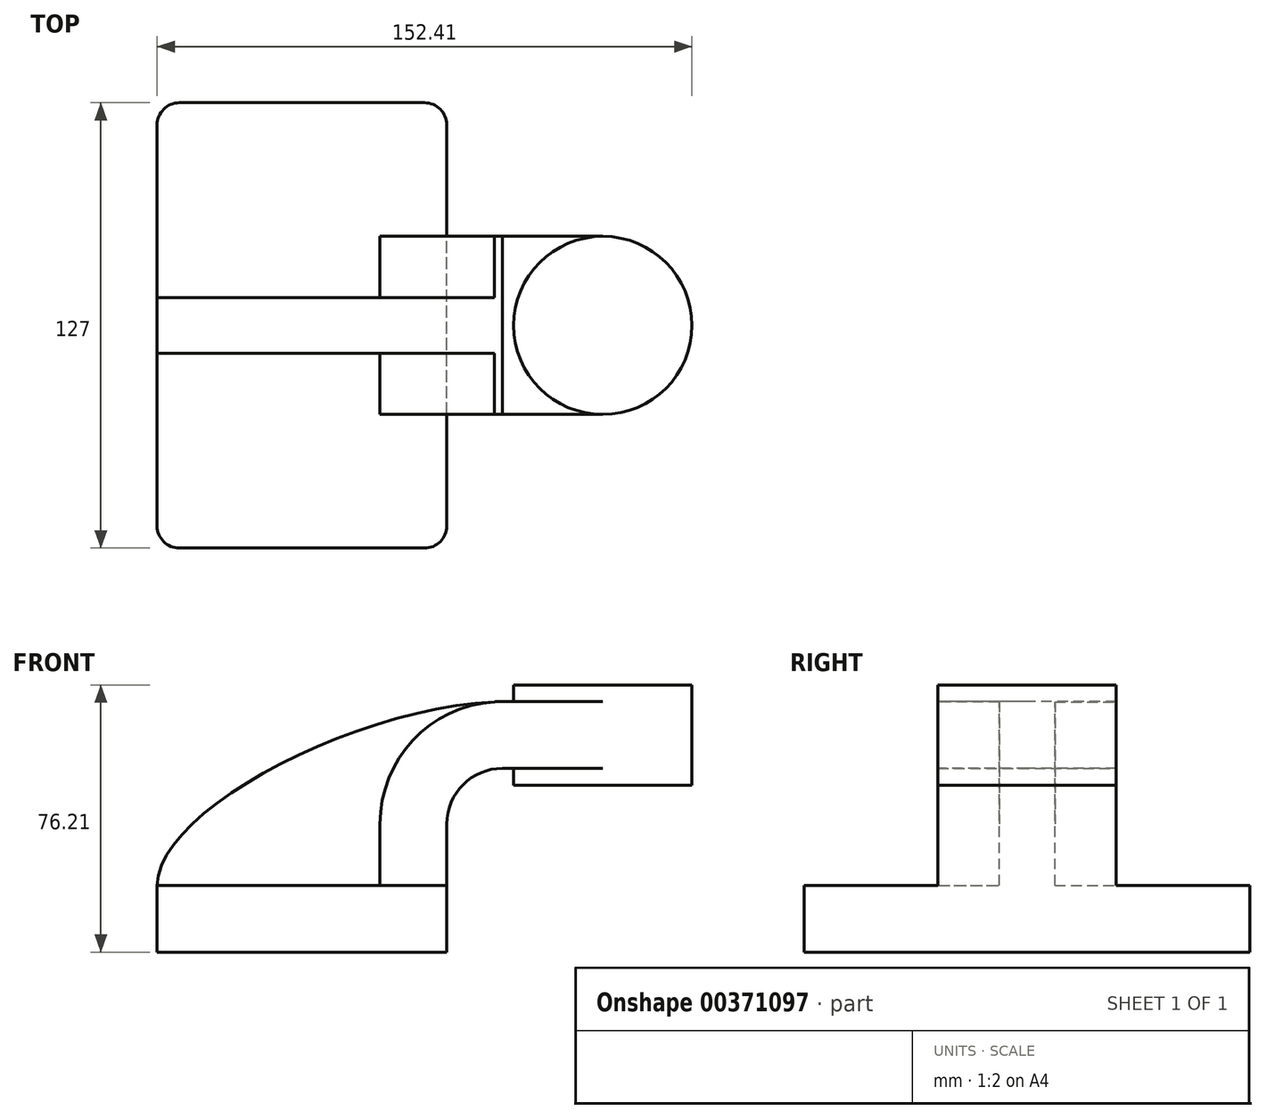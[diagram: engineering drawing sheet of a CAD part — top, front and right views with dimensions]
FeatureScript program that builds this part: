
annotation { "Feature Type Name" : "Feature", "Feature Type Description" : "" }
export const myFeature = defineFeature(function(context is Context, id is Id, definition is map)
    precondition{}
    {
        {
            var Q0;
            Q0=qCreatedBy(makeId("Front.planeOp"),FACE);
            var sketch = newSketch(context, id + "F0", { "sketchPlane" : qUnion([Q0])});
            skLineSegment(sketch, "E0.bottom", {"start": v(41.28, -9.52) * mm, "end": v(-41.28, -9.53) * mm});
            skLineSegment(sketch, "E0.top", {"start": v(41.27, 9.53) * mm, "end": v(-41.28, 9.53) * mm});
            skLineSegment(sketch, "E0.left", {"start": v(41.28, -9.52) * mm, "end": v(41.28, 9.53) * mm});
            skLineSegment(sketch, "E0.right", {"start": v(-41.28, -9.53) * mm, "end": v(-41.28, 9.53) * mm});
            skPoint(sketch, "E0.middle", {"position": v(0, 0) * mm});
            skLineSegment(sketch, "E1.bottom", {"start": v(60.33, 38.1) * mm, "end": v(111.12, 38.1) * mm});
            skLineSegment(sketch, "E1.top", {"start": v(60.33, 66.68) * mm, "end": v(111.12, 66.68) * mm});
            skLineSegment(sketch, "E1.left", {"start": v(60.33, 38.1) * mm, "end": v(60.33, 66.68) * mm});
            skLineSegment(sketch, "E1.right", {"start": v(111.13, 38.1) * mm, "end": v(111.12, 66.68) * mm});
            skPoint(sketch, "E1.middle", {"position": v(85.73, 52.39) * mm});
            skLineSegment(sketch, "E2", {"start": v(41.27, 9.53) * mm, "end": v(41.27, 27) * mm});
            skArc(sketch, "E3", {"start": v(41.28, 27) * mm, "mid": v(45.92, 38.23) * mm, "end": v(57.15, 42.88) * mm});
            skLineSegment(sketch, "E4", {"start": v(57.15, 42.88) * mm, "end": v(85.73, 42.88) * mm});
            skPoint(sketch, "E4.endSnap0", {"position": v(85.73, 38.1) * mm});
            skLineSegment(sketch, "E5.0", {"start": v(57.15, 61.93) * mm, "end": v(85.73, 61.93) * mm});
            skArc(sketch, "E5.1", {"start": v(22.23, 27) * mm, "mid": v(32.45, 51.7) * mm, "end": v(57.15, 61.93) * mm});
            skLineSegment(sketch, "E5.2", {"start": v(22.22, 9.53) * mm, "end": v(22.22, 27) * mm});
            skLineSegment(sketch, "E6", {"start": v(85.73, 38.1) * mm, "end": v(85.72, 66.68) * mm});
            skFitSpline(sketch, "E7", {"points": [v(-41.28, 9.52) * mm, v(57.15, 61.93) * mm], "startDerivative": vector(-0.4, 63.94) * mm, "endDerivative": vector(123, 2.51) * mm});
            skSolve(sketch);
        }
        {
            var Q0;
            Q0=makeQuery(id+"F0.imprint","IMPRINT",FACE,{"disambiguationData":[TD([[makeQuery(id+"F0.imprint","IMPRINT",EDGE,{"derivedFrom":sQuery(id+"F0.wireOp",EDGE,"E0.bottom")}),-1.0]])]});
            extrude(context, id + "F1", {"entities" : qUnion([Q0]), "endBound" : BoundingType.SYMMETRIC, "depth" : 127 * mm});
        }
        {
            var Q0;
            {var subQ1=sQuery(id+"F0.wireOp",EDGE,"E2");Q0=makeQuery(id+"F0.imprint","IMPRINT",FACE,{"disambiguationData":[TD([[makeQuery(id+"F0.imprint","IMPRINT",EDGE,{"derivedFrom":subQ1}),1.0]])]});}
            var Q1;
            {var subQ0=sQuery(id+"F0.wireOp",EDGE,"E4");var subQ1=sQuery(id+"F0.wireOp",EDGE,"E1.left");var subQ2=makeQuery(id+"F0.imprint","INTERSECT",VERTEX,{"derivedFrom":[subQ1,subQ0]});Q1=makeQuery(id+"F0.imprint","IMPRINT",FACE,{"disambiguationData":[TD([[makeQuery(id+"F0.imprint","IMPRINT",EDGE,{"disambiguationData":[TD([[subQ2,-1.0]])],"derivedFrom":subQ1}),-1.0]])]});}
            extrude(context, id + "F2", {"entities" : qUnion([Q0, Q1]), "operationType" : NewBodyOperationType.ADD, "endBound" : BoundingType.SYMMETRIC, "depth" : 50.8 * mm});
        }
        {
            var Q0;
            {var subQ3=sQuery(id+"F0.wireOp",EDGE,"E5.2");Q0=makeQuery(id+"F0.imprint","IMPRINT",FACE,{"disambiguationData":[TD([[makeQuery(id+"F0.imprint","IMPRINT",EDGE,{"derivedFrom":subQ3}),1.0]])]});}
            extrude(context, id + "F3", {"entities" : qUnion([Q0]), "operationType" : NewBodyOperationType.ADD, "endBound" : BoundingType.SYMMETRIC, "depth" : 15.88 * mm});
        }
        {
            var Q0;
            {var subQ4=sQuery(id+"F0.wireOp",EDGE,"E1.right");Q0=makeQuery(id+"F0.imprint","IMPRINT",FACE,{"disambiguationData":[TD([[makeQuery(id+"F0.imprint","IMPRINT",EDGE,{"derivedFrom":subQ4}),1.0]])]});}
            var Q1;
            Q1=sQuery(id+"F0.wireOp",EDGE,"E6");
            revolve(context, id + "F4", {"operationType" : NewBodyOperationType.ADD, "entities" : qUnion([Q0]), "axis" : qUnion([Q1]), "revolveType" : RevolveType.FULL});
        }
        {
            var Q0;
            Q0=makeQuery(id+"F1.opExtrude","CAP_EDGE",EDGE,{"disambiguationData":[OSD([sQuery(id+"F0.wireOp",EDGE,"E0.right")])],"isStart":true});
            var Q1;
            Q1=makeQuery(id+"F1.opExtrude","CAP_EDGE",EDGE,{"disambiguationData":[OSD([sQuery(id+"F0.wireOp",EDGE,"E0.right")])],"isStart":false});
            var Q2;
            Q2=makeQuery(id+"F1.opExtrude","CAP_EDGE",EDGE,{"disambiguationData":[OSD([sQuery(id+"F0.wireOp",EDGE,"E0.left")])],"isStart":false});
            var Q3;
            Q3=makeQuery(id+"F1.opExtrude","CAP_EDGE",EDGE,{"disambiguationData":[OSD([sQuery(id+"F0.wireOp",EDGE,"E0.left")])],"isStart":true});
            fillet(context, id + "F5", {"entities" : qUnion([Q0, Q1, Q2, Q3]), "radius" : 6.35 * mm, "tangentPropagation" : true, "allowEdgeOverflow" : false});
        }
    });
